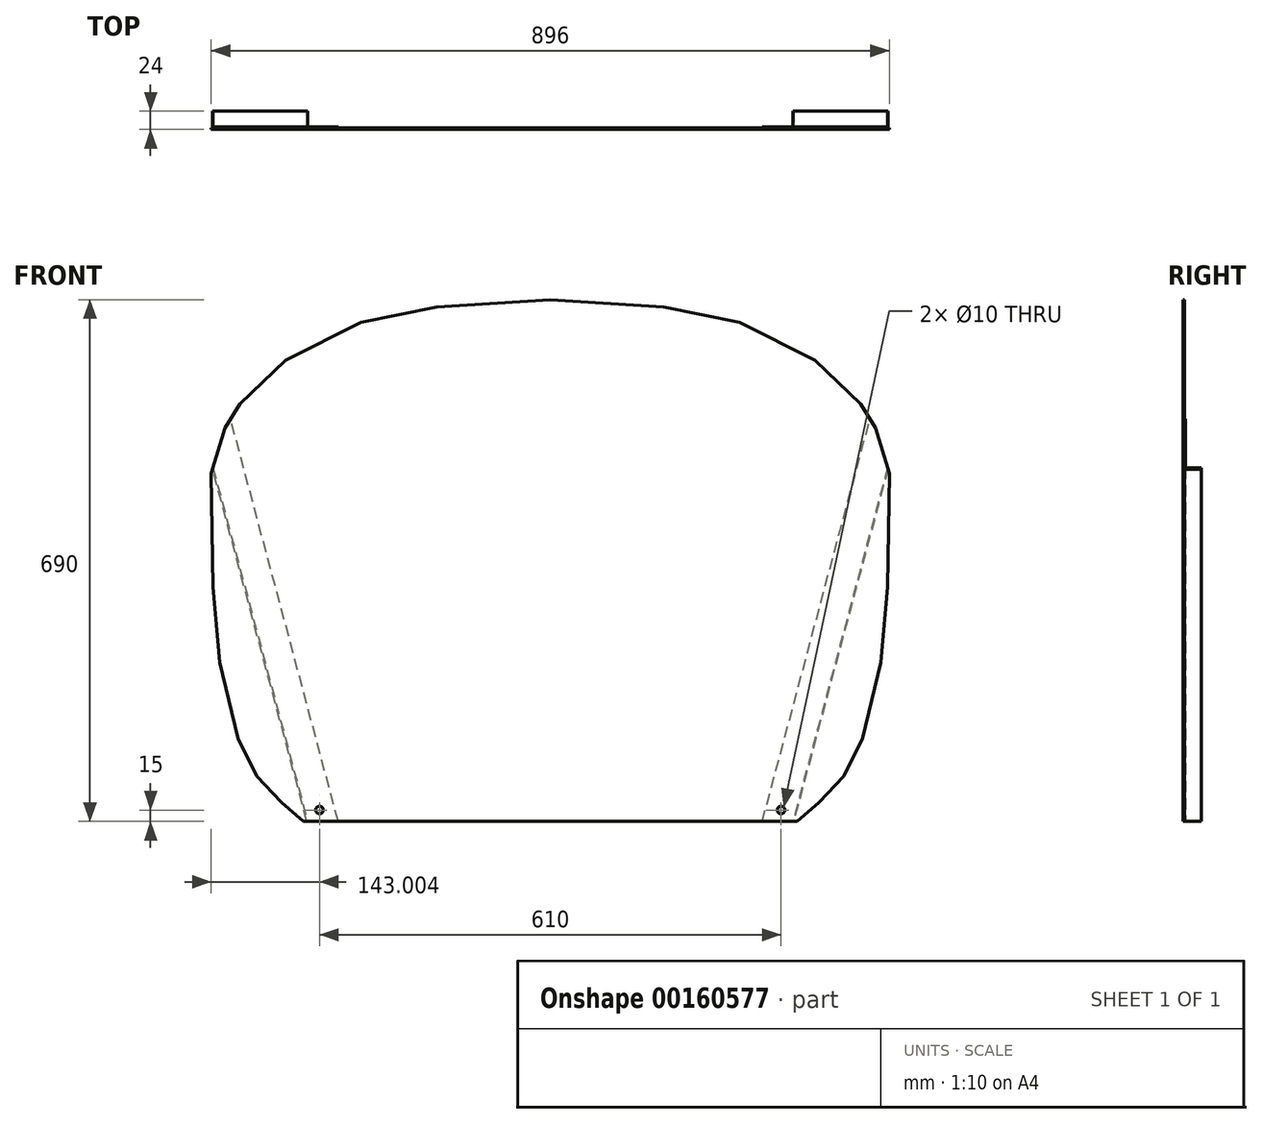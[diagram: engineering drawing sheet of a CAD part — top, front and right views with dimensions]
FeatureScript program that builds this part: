
annotation { "Feature Type Name" : "Feature", "Feature Type Description" : "" }
export const myFeature = defineFeature(function(context is Context, id is Id, definition is map)
    precondition{}
    {
        {
            var Q0;
            Q0=qCreatedBy(makeId("Front.planeOp"),FACE);
            var sketch = newSketch(context, id + "F0", { "sketchPlane" : qUnion([Q0])});
            skLineSegment(sketch, "E0", {"start": v(227.87, -310) * mm, "end": v(227.87, -310) * mm});
            skLineSegment(sketch, "E1", {"start": v(227.87, 380) * mm, "end": v(227.87, 380) * mm});
            skLineSegment(sketch, "E2", {"start": v(-218.13, 0) * mm, "end": v(-209.13, -100) * mm});
            skLineSegment(sketch, "E3", {"start": v(-209.13, -100) * mm, "end": v(-185.13, -200) * mm});
            skLineSegment(sketch, "E4", {"start": v(-160.13, -250) * mm, "end": v(-127.13, -285) * mm});
            skLineSegment(sketch, "E5", {"start": v(-160.13, -250) * mm, "end": v(-185.13, -200) * mm});
            skLineSegment(sketch, "E6", {"start": v(227.87, -310) * mm, "end": v(-98.13, -310) * mm});
            skLineSegment(sketch, "E7", {"start": v(-98.13, -310) * mm, "end": v(-127.13, -285) * mm});
            skLineSegment(sketch, "E8", {"start": v(-202.13, 210) * mm, "end": v(-182.13, 242) * mm});
            skLineSegment(sketch, "E9", {"start": v(-182.13, 242) * mm, "end": v(-122.13, 300) * mm});
            skLineSegment(sketch, "E10", {"start": v(-122.13, 300) * mm, "end": v(-22.13, 350) * mm});
            skLineSegment(sketch, "E11", {"start": v(-22.13, 350) * mm, "end": v(77.87, 370) * mm});
            skLineSegment(sketch, "E12", {"start": v(77.87, 370) * mm, "end": v(227.87, 380) * mm});
            skLineSegment(sketch, "E13", {"start": v(-202.13, 210) * mm, "end": v(-220.13, 150) * mm});
            skLineSegment(sketch, "E14", {"start": v(-220.13, 150) * mm, "end": v(-218.13, 0) * mm, "construction": true});
            skLineSegment(sketch, "E15", {"start": v(-220.13, 150) * mm, "end": v(-218.13, 0) * mm});
            skLineSegment(sketch, "E16.MirrorCS", {"start": v(615.87, -250) * mm, "end": v(582.87, -285) * mm});
            skLineSegment(sketch, "E17.MirrorCS", {"start": v(657.87, 210) * mm, "end": v(637.87, 242) * mm});
            skLineSegment(sketch, "E18.MirrorCS", {"start": v(553.87, -310) * mm, "end": v(582.87, -285) * mm});
            skLineSegment(sketch, "E19.MirrorCS", {"start": v(675.87, 150) * mm, "end": v(673.87, 0) * mm});
            skLineSegment(sketch, "E20.MirrorCS", {"start": v(377.87, 370) * mm, "end": v(227.87, 380) * mm});
            skLineSegment(sketch, "E21.MirrorCS", {"start": v(664.87, -100) * mm, "end": v(640.87, -200) * mm});
            skLineSegment(sketch, "E22.MirrorCS", {"start": v(675.87, 150) * mm, "end": v(673.87, 0) * mm, "construction": true});
            skLineSegment(sketch, "E23.MirrorCS", {"start": v(615.87, -250) * mm, "end": v(640.87, -200) * mm});
            skLineSegment(sketch, "E24.MirrorCS", {"start": v(227.87, -310) * mm, "end": v(553.87, -310) * mm});
            skLineSegment(sketch, "E25.MirrorCS", {"start": v(477.87, 350) * mm, "end": v(377.87, 370) * mm});
            skLineSegment(sketch, "E26.MirrorCS", {"start": v(673.87, 0) * mm, "end": v(664.87, -100) * mm});
            skLineSegment(sketch, "E27.MirrorCS", {"start": v(657.87, 210) * mm, "end": v(675.87, 150) * mm});
            skLineSegment(sketch, "E28.MirrorCS", {"start": v(637.87, 242) * mm, "end": v(577.87, 300) * mm});
            skLineSegment(sketch, "E29.MirrorCS", {"start": v(577.87, 300) * mm, "end": v(477.87, 350) * mm});
            skLineSegment(sketch, "E30", {"start": v(227.87, -310) * mm, "end": v(227.87, -295) * mm, "construction": true});
            skLineSegment(sketch, "E31", {"start": v(227.87, -295) * mm, "end": v(532.87, -295) * mm, "construction": true});
            skLineSegment(sketch, "E32", {"start": v(227.87, -295) * mm, "end": v(-77.13, -295) * mm, "construction": true});
            skLineSegment(sketch, "E33", {"start": v(532.87, -295) * mm, "end": v(532.87, 165) * mm, "construction": true});
            skLineSegment(sketch, "E34", {"start": v(532.87, 165) * mm, "end": v(227.87, 165) * mm, "construction": true});
            skLineSegment(sketch, "E35", {"start": v(227.87, 165) * mm, "end": v(655.87, 165) * mm, "construction": true});
            skLineSegment(sketch, "E36", {"start": v(227.87, 165) * mm, "end": v(-200.13, 165) * mm, "construction": true});
            skLineSegment(sketch, "E37", {"start": v(655.87, 165) * mm, "end": v(532.87, -295) * mm, "construction": true});
            skLineSegment(sketch, "E38", {"start": v(-200.13, 165) * mm, "end": v(-77.13, -295) * mm, "construction": true});
            skLineSegment(sketch, "E39", {"start": v(-52.41, -310) * mm, "end": v(-194.65, 221.96) * mm});
            skLineSegment(sketch, "E40", {"start": v(-93.82, -310) * mm, "end": v(-218.38, 155.83) * mm});
            skLineSegment(sketch, "E41", {"start": v(674.12, 155.83) * mm, "end": v(549.57, -310) * mm});
            skLineSegment(sketch, "E42", {"start": v(508.16, -310) * mm, "end": v(650.4, 221.96) * mm});
            skLineSegment(sketch, "E43", {"start": v(673.58, 157.65) * mm, "end": v(548.53, -310) * mm});
            skLineSegment(sketch, "E44", {"start": v(-217.83, 157.65) * mm, "end": v(-92.78, -310) * mm});
            skCircle(sketch, "E45", {"center": v(-77.13, -295) * mm, "radius": 5 * mm});
            skCircle(sketch, "E46", {"center": v(532.87, -295) * mm, "radius": 5 * mm});
            skSolve(sketch);
        }
        {
            var Q0;
            {var subQ4=sQuery(id+"F0.wireOp",EDGE,"E39");Q0=makeQuery(id+"F0.imprint","IMPRINT",FACE,{"disambiguationData":[TD([[makeQuery(id+"F0.imprint","IMPRINT",EDGE,{"derivedFrom":subQ4}),1.0]])]});}
            var Q1;
            {var subQ0=sQuery(id+"F0.wireOp",EDGE,"E9");Q1=makeQuery(id+"F0.imprint","IMPRINT",FACE,{"disambiguationData":[TD([[makeQuery(id+"F0.imprint","IMPRINT",EDGE,{"derivedFrom":subQ0}),-1.0]])]});}
            var Q2;
            {var subQ0=sQuery(id+"F0.wireOp",EDGE,"E42");Q2=makeQuery(id+"F0.imprint","IMPRINT",FACE,{"disambiguationData":[TD([[makeQuery(id+"F0.imprint","IMPRINT",EDGE,{"derivedFrom":subQ0}),-1.0]])]});}
            var Q3;
            Q3=makeQuery(id+"F0.imprint","IMPRINT",FACE,{"disambiguationData":[TD([[makeQuery(id+"F0.imprint","IMPRINT",EDGE,{"derivedFrom":sQuery(id+"F0.wireOp",EDGE,"E2")}),1.0]])]});
            var Q4;
            Q4=makeQuery(id+"F0.imprint","IMPRINT",FACE,{"disambiguationData":[TD([[makeQuery(id+"F0.imprint","IMPRINT",EDGE,{"derivedFrom":sQuery(id+"F0.wireOp",EDGE,"E16.MirrorCS")}),-1.0]])]});
            var Q5;
            {var subQ0=sQuery(id+"F0.wireOp",EDGE,"E41");Q5=makeQuery(id+"F0.imprint","IMPRINT",FACE,{"disambiguationData":[TD([[makeQuery(id+"F0.imprint","IMPRINT",EDGE,{"derivedFrom":subQ0}),-1.0]])]});}
            var Q6;
            {var subQ0=sQuery(id+"F0.wireOp",EDGE,"E40");Q6=makeQuery(id+"F0.imprint","IMPRINT",FACE,{"disambiguationData":[TD([[makeQuery(id+"F0.imprint","IMPRINT",EDGE,{"derivedFrom":subQ0}),-1.0]])]});}
            extrude(context, id + "F1", {"entities" : qUnion([Q0, Q1, Q2, Q3, Q4, Q5, Q6]), "depth" : 2 * mm});
        }
        {
            var Q0;
            {var subQ0=sQuery(id+"F0.wireOp",EDGE,"E39");Q0=makeQuery(id+"F0.imprint","IMPRINT",FACE,{"disambiguationData":[TD([[makeQuery(id+"F0.imprint","IMPRINT",EDGE,{"derivedFrom":subQ0}),1.0]])]});}
            var Q1;
            {var subQ0=sQuery(id+"F0.wireOp",EDGE,"E42");Q1=makeQuery(id+"F0.imprint","IMPRINT",FACE,{"disambiguationData":[TD([[makeQuery(id+"F0.imprint","IMPRINT",EDGE,{"derivedFrom":subQ0}),-1.0]])]});}
            extrude(context, id + "F2", {"entities" : qUnion([Q0, Q1]), "operationType" : NewBodyOperationType.ADD, "oppositeDirection" : true, "depth" : 1 * mm});
        }
        {
            var Q0;
            {var subQ0=sQuery(id+"F0.wireOp",EDGE,"E41");Q0=makeQuery(id+"F0.imprint","IMPRINT",FACE,{"disambiguationData":[TD([[makeQuery(id+"F0.imprint","IMPRINT",EDGE,{"derivedFrom":subQ0}),-1.0]])]});}
            var Q1;
            {var subQ0=sQuery(id+"F0.wireOp",EDGE,"E40");Q1=makeQuery(id+"F0.imprint","IMPRINT",FACE,{"disambiguationData":[TD([[makeQuery(id+"F0.imprint","IMPRINT",EDGE,{"derivedFrom":subQ0}),-1.0]])]});}
            extrude(context, id + "F3", {"entities" : qUnion([Q0, Q1]), "operationType" : NewBodyOperationType.ADD, "oppositeDirection" : true, "depth" : 22 * mm});
        }
        {
            var Q0;
            Q0=makeQuery(id+"F1.opExtrude","CAP_EDGE",EDGE,{"disambiguationData":[OSD([sQuery(id+"F0.wireOp",EDGE,"E6"),sQuery(id+"F0.wireOp",EDGE,"E24.MirrorCS")])],"isStart":false});
            chamfer(context, id + "F4", {"entities" : qUnion([Q0]), "chamferType" : ChamferType.OFFSET_ANGLE, "width" : 2 * mm, "oppositeDirection" : false, "angle" : 10 * degree, "tangentPropagation" : true});
        }
    });
